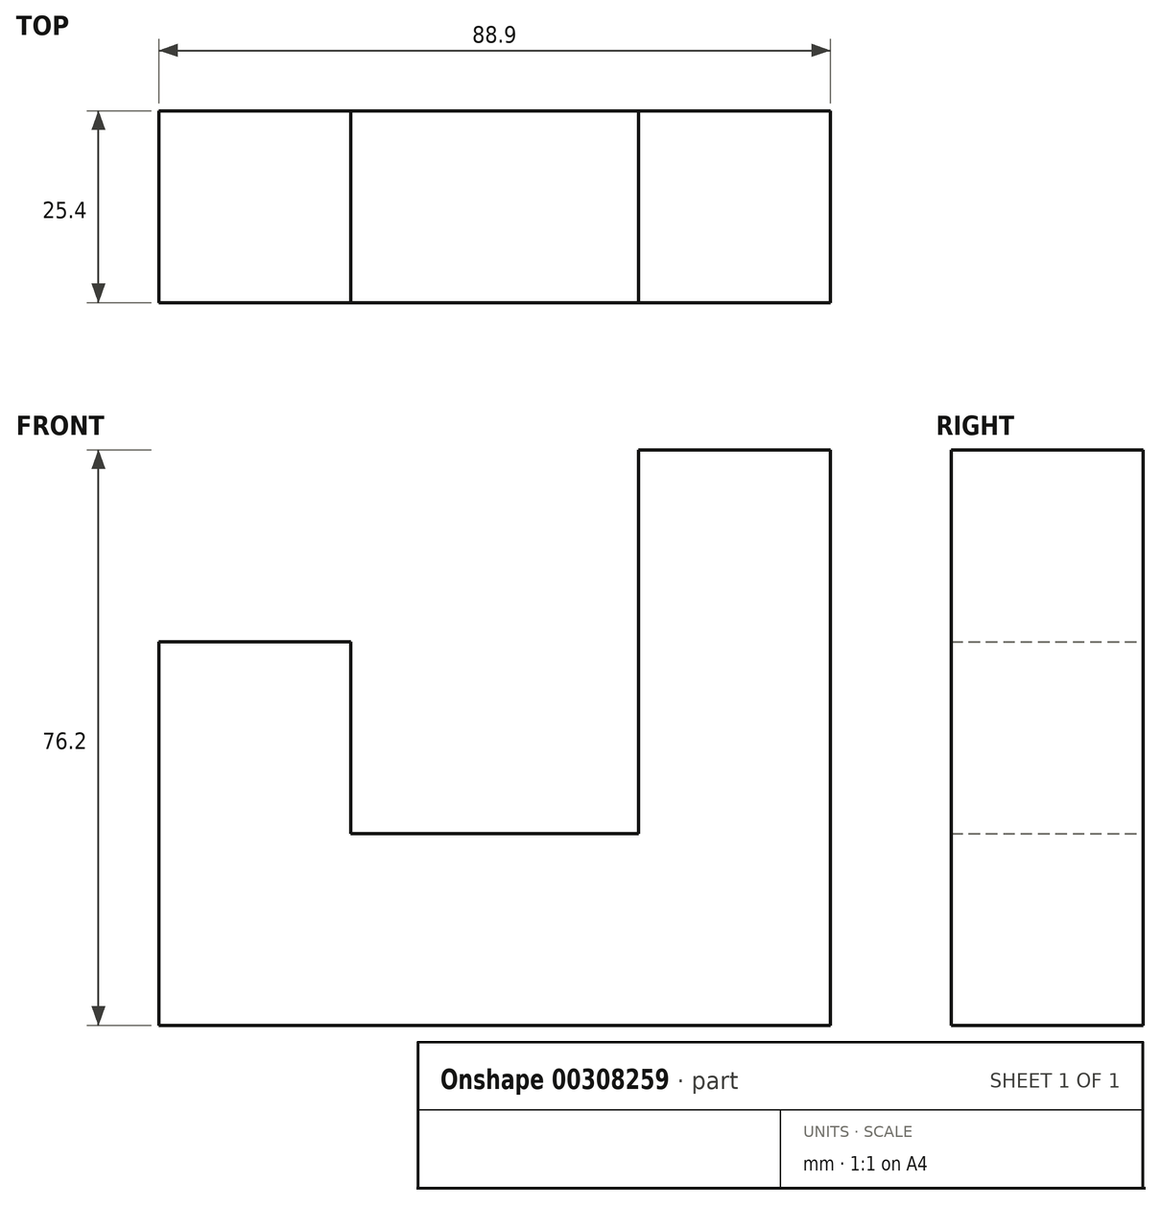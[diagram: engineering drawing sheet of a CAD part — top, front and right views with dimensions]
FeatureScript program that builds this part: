
annotation { "Feature Type Name" : "Feature", "Feature Type Description" : "" }
export const myFeature = defineFeature(function(context is Context, id is Id, definition is map)
    precondition{}
    {
        {
            var Q0;
            Q0=qCreatedBy(makeId("Front.planeOp"),FACE);
            var sketch = newSketch(context, id + "F0", { "sketchPlane" : qUnion([Q0])});
            skLineSegment(sketch, "E0", {"start": v(-42.94, -20.8) * mm, "end": v(45.96, -20.8) * mm});
            skLineSegment(sketch, "E1", {"start": v(45.96, 55.4) * mm, "end": v(20.56, 55.4) * mm});
            skLineSegment(sketch, "E2", {"start": v(20.56, 55.4) * mm, "end": v(20.56, 4.6) * mm});
            skLineSegment(sketch, "E3", {"start": v(20.56, 4.6) * mm, "end": v(-17.54, 4.6) * mm});
            skLineSegment(sketch, "E4", {"start": v(-17.54, 4.6) * mm, "end": v(-17.54, 30) * mm});
            skLineSegment(sketch, "E5", {"start": v(-17.54, 30) * mm, "end": v(-42.94, 30) * mm});
            skLineSegment(sketch, "E6", {"start": v(-42.94, -20.8) * mm, "end": v(-42.94, 30) * mm});
            skLineSegment(sketch, "E7", {"start": v(45.96, 55.4) * mm, "end": v(45.96, -20.8) * mm});
            skSolve(sketch);
        }
        {
            var Q0;
            Q0 = qSketchRegion(id + "F0", true);
            extrude(context, id + "F1", {"entities" : qUnion([Q0]), "depth" : 25.4 * mm});
        }
    });
